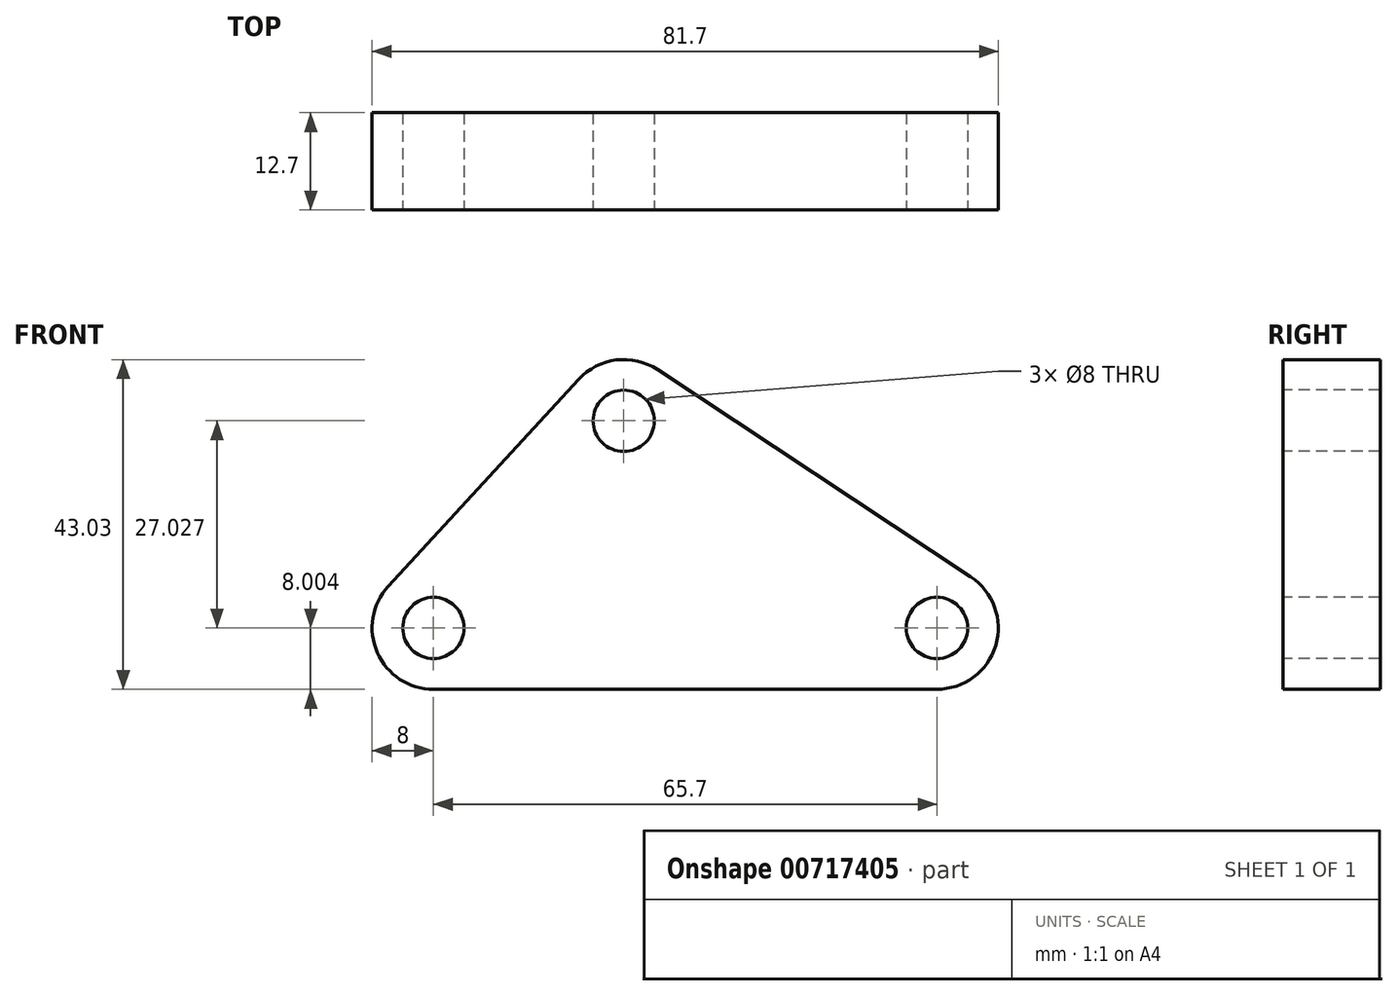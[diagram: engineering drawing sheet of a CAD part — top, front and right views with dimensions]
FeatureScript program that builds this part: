
annotation { "Feature Type Name" : "Feature", "Feature Type Description" : "" }
export const myFeature = defineFeature(function(context is Context, id is Id, definition is map)
    precondition{}
    {
        {
            var Q0;
            Q0=qCreatedBy(makeId("Front.planeOp"),FACE);
            var sketch = newSketch(context, id + "F0", { "sketchPlane" : qUnion([Q0])});
            skLineSegment(sketch, "E0", {"start": v(-16.46, 45.15) * mm, "end": v(-41.29, 18.12) * mm});
            skLineSegment(sketch, "E1", {"start": v(-41.29, 18.12) * mm, "end": v(24.41, 18.12) * mm});
            skLineSegment(sketch, "E2", {"start": v(24.41, 18.12) * mm, "end": v(-16.46, 45.15) * mm});
            skCircle(sketch, "E3", {"center": v(-16.46, 45.15) * mm, "radius": 8 * mm});
            skCircle(sketch, "E4", {"center": v(-41.29, 18.12) * mm, "radius": 8 * mm});
            skCircle(sketch, "E5", {"center": v(24.41, 18.12) * mm, "radius": 8 * mm});
            skLineSegment(sketch, "E6", {"start": v(-41.29, 10.12) * mm, "end": v(24.41, 10.12) * mm});
            skLineSegment(sketch, "E7", {"start": v(28.82, 24.8) * mm, "end": v(-12.05, 51.82) * mm});
            skLineSegment(sketch, "E8", {"start": v(-22.35, 50.56) * mm, "end": v(-47.18, 23.54) * mm});
            skSolve(sketch);
        }
        {
            var Q0;
            {var subQ5=sQuery(id+"F0.wireOp",EDGE,"E8");Q0=makeQuery(id+"F0.imprint","IMPRINT",FACE,{"disambiguationData":[TD([[makeQuery(id+"F0.imprint","IMPRINT",EDGE,{"derivedFrom":subQ5}),1.0]])]});}
            var Q1;
            {var subQ3=sQuery(id+"F0.wireOp",EDGE,"E2");var subQ4=sQuery(id+"F0.wireOp",EDGE,"E0");var subQ5=makeQuery(id+"F0.imprint","INTERSECT",VERTEX,{"derivedFrom":[subQ4,subQ3]});Q1=makeQuery(id+"F0.imprint","IMPRINT",FACE,{"disambiguationData":[TD([[makeQuery(id+"F0.imprint","IMPRINT",EDGE,{"disambiguationData":[TD([[subQ5,-1.0]])],"derivedFrom":subQ4}),-1.0]])]});}
            var Q2;
            {var subQ3=sQuery(id+"F0.wireOp",EDGE,"E3");var subQ9=sQuery(id+"F0.wireOp",EDGE,"E0");var subQ10=makeQuery(id+"F0.imprint","INTERSECT",VERTEX,{"derivedFrom":[subQ9,subQ3]});Q2=makeQuery(id+"F0.imprint","IMPRINT",FACE,{"disambiguationData":[TD([[makeQuery(id+"F0.imprint","IMPRINT",EDGE,{"disambiguationData":[TD([[subQ10,-1.0]])],"derivedFrom":subQ9}),1.0]])]});}
            var Q3;
            {var subQ0=sQuery(id+"F0.wireOp",EDGE,"E2");var subQ1=sQuery(id+"F0.wireOp",EDGE,"E0");var subQ2=makeQuery(id+"F0.imprint","INTERSECT",VERTEX,{"derivedFrom":[subQ1,subQ0]});Q3=makeQuery(id+"F0.imprint","IMPRINT",FACE,{"disambiguationData":[TD([[makeQuery(id+"F0.imprint","IMPRINT",EDGE,{"disambiguationData":[TD([[subQ2,-1.0]])],"derivedFrom":subQ1}),1.0]])]});}
            var Q4;
            {var subQ5=sQuery(id+"F0.wireOp",EDGE,"E7");Q4=makeQuery(id+"F0.imprint","IMPRINT",FACE,{"disambiguationData":[TD([[makeQuery(id+"F0.imprint","IMPRINT",EDGE,{"derivedFrom":subQ5}),1.0]])]});}
            var Q5;
            {var subQ2=sQuery(id+"F0.wireOp",EDGE,"E1");var subQ5=sQuery(id+"F0.wireOp",EDGE,"E2");var subQ7=makeQuery(id+"F0.imprint","INTERSECT",VERTEX,{"derivedFrom":[subQ2,subQ5]});Q5=makeQuery(id+"F0.imprint","IMPRINT",FACE,{"disambiguationData":[TD([[makeQuery(id+"F0.imprint","IMPRINT",EDGE,{"disambiguationData":[TD([[subQ7,1.0]])],"derivedFrom":subQ2}),-1.0]])]});}
            var Q6;
            {var subQ0=sQuery(id+"F0.wireOp",EDGE,"E2");var subQ1=sQuery(id+"F0.wireOp",EDGE,"E1");var subQ2=makeQuery(id+"F0.imprint","INTERSECT",VERTEX,{"derivedFrom":[subQ1,subQ0]});Q6=makeQuery(id+"F0.imprint","IMPRINT",FACE,{"disambiguationData":[TD([[makeQuery(id+"F0.imprint","IMPRINT",EDGE,{"disambiguationData":[TD([[subQ2,1.0]])],"derivedFrom":subQ1}),1.0]])]});}
            var Q7;
            {var subQ5=sQuery(id+"F0.wireOp",EDGE,"E6");Q7=makeQuery(id+"F0.imprint","IMPRINT",FACE,{"disambiguationData":[TD([[makeQuery(id+"F0.imprint","IMPRINT",EDGE,{"derivedFrom":subQ5}),1.0]])]});}
            var Q8;
            {var subQ3=sQuery(id+"F0.wireOp",EDGE,"E1");var subQ4=sQuery(id+"F0.wireOp",EDGE,"E0");var subQ5=makeQuery(id+"F0.imprint","INTERSECT",VERTEX,{"derivedFrom":[subQ4,subQ3]});Q8=makeQuery(id+"F0.imprint","IMPRINT",FACE,{"disambiguationData":[TD([[makeQuery(id+"F0.imprint","IMPRINT",EDGE,{"disambiguationData":[TD([[subQ5,1.0]])],"derivedFrom":subQ4}),-1.0]])]});}
            var Q9;
            {var subQ0=sQuery(id+"F0.wireOp",EDGE,"E1");var subQ1=sQuery(id+"F0.wireOp",EDGE,"E0");var subQ2=makeQuery(id+"F0.imprint","INTERSECT",VERTEX,{"derivedFrom":[subQ1,subQ0]});Q9=makeQuery(id+"F0.imprint","IMPRINT",FACE,{"disambiguationData":[TD([[makeQuery(id+"F0.imprint","IMPRINT",EDGE,{"disambiguationData":[TD([[subQ2,1.0]])],"derivedFrom":subQ1}),1.0]])]});}
            extrude(context, id + "F1", {"entities" : qUnion([Q0, Q1, Q2, Q3, Q4, Q5, Q6, Q7, Q8, Q9]), "depth" : 12.7 * mm, "offsetDistance" : 25.4 * mm});
        }
        {
            var Q0;
            Q0=makeQuery(id+"F1.opExtrude","CAP_FACE",FACE,{"disambiguationData":[OSD([sQuery(id+"F0.wireOp",EDGE,"E3"),sQuery(id+"F0.wireOp",EDGE,"E4"),sQuery(id+"F0.wireOp",EDGE,"E5"),sQuery(id+"F0.wireOp",EDGE,"E6"),sQuery(id+"F0.wireOp",EDGE,"E7"),sQuery(id+"F0.wireOp",EDGE,"E8")])],"isStart":false});
            var sketch = newSketch(context, id + "F2", { "sketchPlane" : qUnion([Q0])});
            skCircle(sketch, "E9", {"center": v(-41.29, 18.12) * mm, "radius": 4 * mm});
            skCircle(sketch, "E10", {"center": v(-16.46, 45.15) * mm, "radius": 4 * mm});
            skCircle(sketch, "E11", {"center": v(24.41, 18.12) * mm, "radius": 4 * mm});
            skSolve(sketch);
        }
        {
            var Q0;
            Q0=makeQuery(id+"F2.imprint","IMPRINT",FACE,{"disambiguationData":[TD([[makeQuery(id+"F2.imprint","IMPRINT",EDGE,{"derivedFrom":sQuery(id+"F2.wireOp",EDGE,"E10")}),1.0]])]});
            var Q1;
            Q1=makeQuery(id+"F2.imprint","IMPRINT",FACE,{"disambiguationData":[TD([[makeQuery(id+"F2.imprint","IMPRINT",EDGE,{"derivedFrom":sQuery(id+"F2.wireOp",EDGE,"E9")}),1.0]])]});
            var Q2;
            Q2=makeQuery(id+"F2.imprint","IMPRINT",FACE,{"disambiguationData":[TD([[makeQuery(id+"F2.imprint","IMPRINT",EDGE,{"derivedFrom":sQuery(id+"F2.wireOp",EDGE,"E11")}),1.0]])]});
            extrude(context, id + "F3", {"entities" : qUnion([Q0, Q1, Q2]), "operationType" : NewBodyOperationType.REMOVE, "endBound" : BoundingType.UP_TO_NEXT, "oppositeDirection" : true, "depth" : 25.4 * mm, "offsetDistance" : 25.4 * mm});
        }
    });
